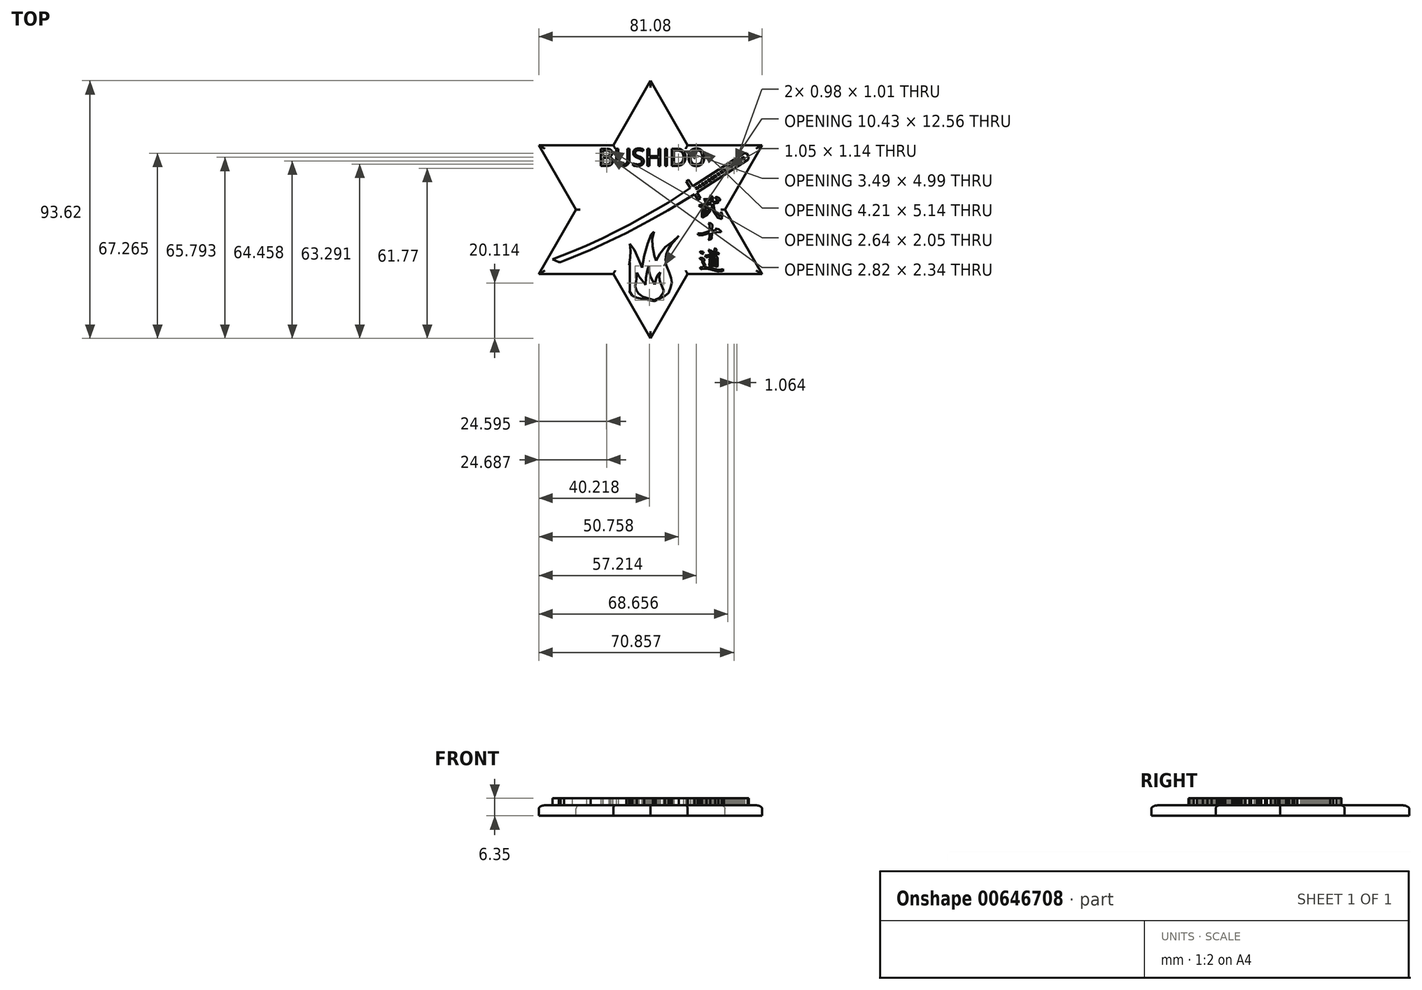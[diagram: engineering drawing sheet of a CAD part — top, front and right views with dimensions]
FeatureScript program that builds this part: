
annotation { "Feature Type Name" : "Feature", "Feature Type Description" : "" }
export const myFeature = defineFeature(function(context is Context, id is Id, definition is map)
    precondition{}
    {
        {
            var Q0;
            Q0=qCreatedBy(makeId("Top.planeOp"),FACE);
            var sketch = newSketch(context, id + "F0", { "sketchPlane" : qUnion([Q0])});
            skLineSegment(sketch, "E0.0", {"start": v(40.54, -23.4) * mm, "end": v(13.51, -23.4) * mm});
            skLineSegment(sketch, "E0.1", {"start": v(-40.54, -23.4) * mm, "end": v(-27.02, 0) * mm});
            skLineSegment(sketch, "E0.2", {"start": v(0, 46.8) * mm, "end": v(13.51, 23.4) * mm});
            skPoint(sketch, "E0.0.midPoint", {"position": v(0, -23.4) * mm});
            skLineSegment(sketch, "E1.0", {"start": v(-40.54, 23.4) * mm, "end": v(-13.51, 23.4) * mm});
            skLineSegment(sketch, "E1.1", {"start": v(40.54, 23.4) * mm, "end": v(27.02, 0) * mm});
            skLineSegment(sketch, "E1.2", {"start": v(0, -46.8) * mm, "end": v(-13.51, -23.4) * mm});
            skPoint(sketch, "E1.0.midPoint", {"position": v(0, 23.4) * mm});
            skPoint(sketch, "E0.cCircle.center.orphan", {"position": v(0, 0) * mm});
            skLineSegment(sketch, "E2.trimOffspring", {"start": v(13.51, -23.4) * mm, "end": v(0, -46.8) * mm});
            skLineSegment(sketch, "E3.trimOffspring", {"start": v(27.02, 0) * mm, "end": v(40.54, -23.4) * mm});
            skLineSegment(sketch, "E4.trimOffspring", {"start": v(13.51, 23.4) * mm, "end": v(40.54, 23.4) * mm});
            skLineSegment(sketch, "E5.trimOffspring", {"start": v(-13.51, 23.4) * mm, "end": v(0, 46.8) * mm});
            skLineSegment(sketch, "E6.trimOffspring", {"start": v(-27.02, 0) * mm, "end": v(-40.54, 23.4) * mm});
            skLineSegment(sketch, "E7.trimOffspring", {"start": v(-13.51, -23.4) * mm, "end": v(-40.54, -23.4) * mm});
            skSolve(sketch);
        }
        {
            var Q0;
            Q0=qCreatedBy(makeId("Top.planeOp"),FACE);
            var sketch = newSketch(context, id + "F1", { "sketchPlane" : qUnion([Q0])});
            skText(sketch, "E8", { "text": "BUSHIDO", "fontName": "OpenSans-Regular.ttf"});
            const initialGuessF1  = {"E8": [-0.01885, 0.01586, 1, 0, 0.0063]};
            skSetInitialGuess(sketch, initialGuessF1);
            skSolve(sketch);
        }
        {
            var Q0;
            Q0=qCreatedBy(makeId("Top.planeOp"),FACE);
            var sketch = newSketch(context, id + "F2", { "sketchPlane" : qUnion([Q0])});
            skLineSegment(sketch, "E9", {"start": v(15.34, 8.47) * mm, "end": v(33.88, 20.46) * mm});
            skLineSegment(sketch, "E10", {"start": v(33.88, 20.46) * mm, "end": v(34.92, 20.37) * mm});
            skLineSegment(sketch, "E11", {"start": v(34.92, 20.37) * mm, "end": v(35.66, 19.22) * mm});
            skLineSegment(sketch, "E12", {"start": v(35.66, 19.22) * mm, "end": v(35.4, 18.12) * mm});
            skLineSegment(sketch, "E13", {"start": v(35.4, 18.12) * mm, "end": v(16.85, 6.14) * mm});
            skLineSegment(sketch, "E14", {"start": v(12.95, 10.24) * mm, "end": v(13.83, 10.8) * mm});
            skLineSegment(sketch, "E15", {"start": v(13.83, 10.8) * mm, "end": v(18.2, 4.04) * mm});
            skLineSegment(sketch, "E16", {"start": v(18.2, 4.04) * mm, "end": v(17.3, 3.5) * mm});
            skLineSegment(sketch, "E17", {"start": v(17.3, 3.5) * mm, "end": v(12.95, 10.24) * mm});
            skLineSegment(sketch, "E18", {"start": v(16.55, 8.25) * mm, "end": v(16.34, 7.6) * mm});
            skLineSegment(sketch, "E19", {"start": v(16.34, 7.6) * mm, "end": v(17.21, 7.33) * mm});
            skLineSegment(sketch, "E20", {"start": v(17.21, 7.33) * mm, "end": v(17.4, 7.9) * mm});
            skLineSegment(sketch, "E21", {"start": v(17.4, 7.9) * mm, "end": v(16.55, 8.25) * mm});
            skLineSegment(sketch, "E22", {"start": v(17.65, 8.97) * mm, "end": v(17.54, 8.22) * mm});
            skLineSegment(sketch, "E23", {"start": v(17.54, 8.22) * mm, "end": v(18.43, 8.09) * mm});
            skLineSegment(sketch, "E24", {"start": v(18.43, 8.09) * mm, "end": v(18.51, 8.64) * mm});
            skLineSegment(sketch, "E25", {"start": v(18.51, 8.64) * mm, "end": v(17.65, 8.97) * mm});
            skLineSegment(sketch, "E26", {"start": v(18.82, 9.72) * mm, "end": v(18.74, 8.83) * mm});
            skLineSegment(sketch, "E27", {"start": v(18.74, 8.83) * mm, "end": v(19.57, 8.76) * mm});
            skLineSegment(sketch, "E28", {"start": v(19.57, 8.76) * mm, "end": v(19.62, 9.43) * mm});
            skLineSegment(sketch, "E29", {"start": v(19.62, 9.43) * mm, "end": v(18.82, 9.72) * mm});
            skLineSegment(sketch, "E30", {"start": v(19.9, 10.43) * mm, "end": v(19.88, 9.68) * mm});
            skLineSegment(sketch, "E31", {"start": v(19.88, 9.68) * mm, "end": v(20.51, 9.4) * mm});
            skLineSegment(sketch, "E32", {"start": v(20.51, 9.4) * mm, "end": v(20.58, 10.1) * mm});
            skLineSegment(sketch, "E33", {"start": v(20.58, 10.1) * mm, "end": v(19.9, 10.43) * mm});
            skLineSegment(sketch, "E34", {"start": v(21.02, 11.14) * mm, "end": v(20.9, 10.44) * mm});
            skLineSegment(sketch, "E35", {"start": v(20.9, 10.44) * mm, "end": v(21.67, 10.1) * mm});
            skLineSegment(sketch, "E36", {"start": v(21.67, 10.1) * mm, "end": v(21.93, 10.69) * mm});
            skLineSegment(sketch, "E37", {"start": v(21.93, 10.69) * mm, "end": v(21.02, 11.14) * mm});
            skLineSegment(sketch, "E38", {"start": v(22.13, 11.86) * mm, "end": v(21.96, 11.15) * mm});
            skLineSegment(sketch, "E39", {"start": v(21.96, 11.15) * mm, "end": v(22.82, 10.95) * mm});
            skLineSegment(sketch, "E40", {"start": v(22.82, 10.95) * mm, "end": v(22.97, 11.51) * mm});
            skLineSegment(sketch, "E41", {"start": v(22.97, 11.51) * mm, "end": v(22.13, 11.86) * mm});
            skLineSegment(sketch, "E42", {"start": v(23.24, 12.58) * mm, "end": v(23.05, 11.94) * mm});
            skLineSegment(sketch, "E43", {"start": v(23.05, 11.94) * mm, "end": v(23.85, 11.7) * mm});
            skLineSegment(sketch, "E44", {"start": v(23.85, 11.7) * mm, "end": v(24, 12.2) * mm});
            skLineSegment(sketch, "E45", {"start": v(24, 12.2) * mm, "end": v(23.24, 12.58) * mm});
            skLineSegment(sketch, "E46", {"start": v(24.42, 13.34) * mm, "end": v(24.27, 12.62) * mm});
            skLineSegment(sketch, "E47", {"start": v(24.27, 12.62) * mm, "end": v(25, 12.46) * mm});
            skLineSegment(sketch, "E48", {"start": v(25, 12.46) * mm, "end": v(25.16, 12.95) * mm});
            skLineSegment(sketch, "E49", {"start": v(25.16, 12.95) * mm, "end": v(24.42, 13.34) * mm});
            skLineSegment(sketch, "E50", {"start": v(25.56, 14.13) * mm, "end": v(25.36, 13.44) * mm});
            skLineSegment(sketch, "E51", {"start": v(25.36, 13.44) * mm, "end": v(26.18, 13.2) * mm});
            skLineSegment(sketch, "E52", {"start": v(26.18, 13.2) * mm, "end": v(26.34, 13.78) * mm});
            skLineSegment(sketch, "E53", {"start": v(26.34, 13.78) * mm, "end": v(25.56, 14.13) * mm});
            skLineSegment(sketch, "E54", {"start": v(26.77, 14.86) * mm, "end": v(26.5, 14.15) * mm});
            skLineSegment(sketch, "E55", {"start": v(26.5, 14.15) * mm, "end": v(27.17, 13.9) * mm});
            skLineSegment(sketch, "E56", {"start": v(27.17, 13.9) * mm, "end": v(27.39, 14.47) * mm});
            skLineSegment(sketch, "E57", {"start": v(27.39, 14.47) * mm, "end": v(26.77, 14.86) * mm});
            skLineSegment(sketch, "E58", {"start": v(27.8, 15.53) * mm, "end": v(27.6, 14.77) * mm});
            skLineSegment(sketch, "E59", {"start": v(27.6, 14.77) * mm, "end": v(28.27, 14.4) * mm});
            skLineSegment(sketch, "E60", {"start": v(28.27, 14.4) * mm, "end": v(28.64, 15.06) * mm});
            skLineSegment(sketch, "E61", {"start": v(28.64, 15.06) * mm, "end": v(27.8, 15.53) * mm});
            skLineSegment(sketch, "E62", {"start": v(28.9, 16.23) * mm, "end": v(28.62, 15.49) * mm});
            skLineSegment(sketch, "E63", {"start": v(28.62, 15.49) * mm, "end": v(29.33, 15.22) * mm});
            skLineSegment(sketch, "E64", {"start": v(29.33, 15.22) * mm, "end": v(29.57, 15.87) * mm});
            skLineSegment(sketch, "E65", {"start": v(29.57, 15.87) * mm, "end": v(28.9, 16.23) * mm});
            skLineSegment(sketch, "E66", {"start": v(30.06, 16.99) * mm, "end": v(29.83, 16.21) * mm});
            skLineSegment(sketch, "E67", {"start": v(29.83, 16.21) * mm, "end": v(30.61, 15.98) * mm});
            skLineSegment(sketch, "E68", {"start": v(30.61, 15.98) * mm, "end": v(30.8, 16.62) * mm});
            skLineSegment(sketch, "E69", {"start": v(30.8, 16.62) * mm, "end": v(30.06, 16.99) * mm});
            skLineSegment(sketch, "E70", {"start": v(31.23, 17.74) * mm, "end": v(30.89, 17.09) * mm});
            skLineSegment(sketch, "E71", {"start": v(30.89, 17.09) * mm, "end": v(31.59, 16.73) * mm});
            skLineSegment(sketch, "E72", {"start": v(31.59, 16.73) * mm, "end": v(31.87, 17.27) * mm});
            skLineSegment(sketch, "E73", {"start": v(31.87, 17.27) * mm, "end": v(31.23, 17.74) * mm});
            skLineSegment(sketch, "E74", {"start": v(32.3, 18.43) * mm, "end": v(31.96, 17.78) * mm});
            skLineSegment(sketch, "E75", {"start": v(31.96, 17.78) * mm, "end": v(32.67, 17.4) * mm});
            skLineSegment(sketch, "E76", {"start": v(32.67, 17.4) * mm, "end": v(32.98, 17.98) * mm});
            skLineSegment(sketch, "E77", {"start": v(32.98, 17.98) * mm, "end": v(32.3, 18.43) * mm});
            skPoint(sketch, "E78.orphan", {"position": v(32.32, 18.44) * mm});
            skLineSegment(sketch, "E79", {"start": v(33.35, 19.2) * mm, "end": v(33.15, 18.54) * mm});
            skPoint(sketch, "E79.endSnap0", {"position": v(31.55, 17.5) * mm});
            skLineSegment(sketch, "E80", {"start": v(33.15, 18.54) * mm, "end": v(33.88, 18.06) * mm});
            skLineSegment(sketch, "E81", {"start": v(33.88, 18.06) * mm, "end": v(34.12, 18.82) * mm});
            skLineSegment(sketch, "E82", {"start": v(34.12, 18.82) * mm, "end": v(33.35, 19.2) * mm});
            skLineSegment(sketch, "E83", {"start": v(14.46, 7.9) * mm, "end": v(13.44, 5.95) * mm});
            skLineSegment(sketch, "E84", {"start": v(13.44, 5.95) * mm, "end": v(15.97, 5.57) * mm});
            skLineSegment(sketch, "E85", {"start": v(15.97, 5.57) * mm, "end": v(13.5, 3.98) * mm});
            skLineSegment(sketch, "E86", {"start": v(13.5, 3.98) * mm, "end": v(6.4, -0.24) * mm});
            skLineSegment(sketch, "E87", {"start": v(6.4, -0.24) * mm, "end": v(0.58, -3.5) * mm});
            skLineSegment(sketch, "E88", {"start": v(0.58, -3.5) * mm, "end": v(-8.8, -8.5) * mm});
            skLineSegment(sketch, "E89", {"start": v(-8.8, -8.5) * mm, "end": v(-21.7, -14.6) * mm});
            skLineSegment(sketch, "E90", {"start": v(-21.7, -14.6) * mm, "end": v(-31.4, -18.56) * mm});
            skLineSegment(sketch, "E91", {"start": v(-31.4, -18.56) * mm, "end": v(-32.66, -19.03) * mm});
            skLineSegment(sketch, "E92", {"start": v(-32.66, -19.03) * mm, "end": v(-33.3, -19.1) * mm});
            skLineSegment(sketch, "E93", {"start": v(-33.3, -19.1) * mm, "end": v(-35.54, -18.07) * mm});
            skLineSegment(sketch, "E94", {"start": v(-35.54, -18.07) * mm, "end": v(-28.42, -15.3) * mm});
            skLineSegment(sketch, "E95", {"start": v(-28.42, -15.3) * mm, "end": v(-23.22, -13.07) * mm});
            skLineSegment(sketch, "E96", {"start": v(-23.22, -13.07) * mm, "end": v(-17.44, -10.38) * mm});
            skLineSegment(sketch, "E97", {"start": v(-17.44, -10.38) * mm, "end": v(-12.94, -8.11) * mm});
            skLineSegment(sketch, "E98", {"start": v(-12.94, -8.11) * mm, "end": v(-7.67, -5.44) * mm});
            skLineSegment(sketch, "E99", {"start": v(-7.67, -5.44) * mm, "end": v(-3.24, -2.96) * mm});
            skLineSegment(sketch, "E100", {"start": v(-3.24, -2.96) * mm, "end": v(2.18, 0.08) * mm});
            skLineSegment(sketch, "E101", {"start": v(2.18, 0.08) * mm, "end": v(6.48, 2.49) * mm});
            skLineSegment(sketch, "E102", {"start": v(6.48, 2.49) * mm, "end": v(14.46, 7.9) * mm});
            skLineSegment(sketch, "E103", {"start": v(13.44, 5.95) * mm, "end": v(7.48, 2.47) * mm});
            skLineSegment(sketch, "E104", {"start": v(7.48, 2.47) * mm, "end": v(0.03, -1.9) * mm});
            skLineSegment(sketch, "E105", {"start": v(0.03, -1.9) * mm, "end": v(-3.12, -3.67) * mm});
            skLineSegment(sketch, "E106", {"start": v(-3.12, -3.67) * mm, "end": v(-6.95, -5.81) * mm});
            skLineSegment(sketch, "E107", {"start": v(-6.95, -5.81) * mm, "end": v(-10.18, -7.44) * mm});
            skLineSegment(sketch, "E108", {"start": v(-10.18, -7.44) * mm, "end": v(-13.58, -9.15) * mm});
            skLineSegment(sketch, "E109", {"start": v(-13.58, -9.15) * mm, "end": v(-19.43, -12.06) * mm});
            skLineSegment(sketch, "E110", {"start": v(-19.43, -12.06) * mm, "end": v(-23.74, -14.07) * mm});
            skLineSegment(sketch, "E111", {"start": v(-23.74, -14.07) * mm, "end": v(-29.14, -16.33) * mm});
            skLineSegment(sketch, "E112", {"start": v(-29.14, -16.33) * mm, "end": v(-32.88, -17.72) * mm});
            skLineSegment(sketch, "E113", {"start": v(-32.88, -17.72) * mm, "end": v(-35.54, -18.07) * mm});
            skLineSegment(sketch, "E114.0", {"start": v(14.46, 7.9) * mm, "end": v(15.34, 8.47) * mm, "construction": true});
            skLineSegment(sketch, "E115.0", {"start": v(16.55, 8.25) * mm, "end": v(32.32, 18.44) * mm, "construction": true});
            skLineSegment(sketch, "E116.0", {"start": v(31.55, 17.5) * mm, "end": v(33.15, 18.54) * mm, "construction": true});
            skLineSegment(sketch, "E117.0", {"start": v(15.97, 5.57) * mm, "end": v(16.85, 6.14) * mm, "construction": true});
            skLineSegment(sketch, "E118.0", {"start": v(7.48, 2.47) * mm, "end": v(33.35, 19.2) * mm, "construction": true});
            skLineSegment(sketch, "E119.0", {"start": v(-10.18, -7.44) * mm, "end": v(-3.24, -2.96) * mm, "construction": true});
            skLineSegment(sketch, "E120.0", {"start": v(15.34, 8.47) * mm, "end": v(13.83, 10.8) * mm, "construction": true});
            skLineSegment(sketch, "E121.0", {"start": v(17.3, 3.5) * mm, "end": v(12.95, 10.24) * mm, "construction": true});
            skSolve(sketch);
        }
        {
            var Q0;
            Q0=qCreatedBy(makeId("Top.planeOp"),FACE);
            var sketch = newSketch(context, id + "F3", { "sketchPlane" : qUnion([Q0])});
            skFitSpline(sketch, "E122", {"points": [v(19.27, 3.7) * mm, v(21.47, 3.65) * mm, v(19.77, 2.87) * mm, v(20.16, 3.2) * mm, v(19.27, 3.7) * mm]});
            skFitSpline(sketch, "E123", {"points": [v(23.53, 4.38) * mm, v(25, 3.2) * mm, v(25.02, 4.08) * mm, v(23.53, 4.38) * mm]});
            skLineSegment(sketch, "E124", {"start": v(21.52, 5.11) * mm, "end": v(22.2, 4.96) * mm});
            skLineSegment(sketch, "E125", {"start": v(22.2, 4.96) * mm, "end": v(22.65, 4.52) * mm});
            skLineSegment(sketch, "E126", {"start": v(22.65, 4.52) * mm, "end": v(22.65, 2.8) * mm});
            skLineSegment(sketch, "E127", {"start": v(22.65, 2.8) * mm, "end": v(24.31, 3.08) * mm});
            skLineSegment(sketch, "E128", {"start": v(24.31, 3.08) * mm, "end": v(24.79, 2.72) * mm});
            skLineSegment(sketch, "E129", {"start": v(24.79, 2.72) * mm, "end": v(24.2, 2.4) * mm});
            skLineSegment(sketch, "E130", {"start": v(24.2, 2.4) * mm, "end": v(22.86, 2.14) * mm});
            skLineSegment(sketch, "E131", {"start": v(22.86, 2.14) * mm, "end": v(23.31, -0.3) * mm});
            skLineSegment(sketch, "E132", {"start": v(23.31, -0.3) * mm, "end": v(25.29, -2.58) * mm});
            skLineSegment(sketch, "E133", {"start": v(25.29, -2.58) * mm, "end": v(25.61, -1.7) * mm});
            skLineSegment(sketch, "E134", {"start": v(25.61, -1.7) * mm, "end": v(25.61, -0.75) * mm});
            skLineSegment(sketch, "E135", {"start": v(25.61, -0.75) * mm, "end": v(26.1, -1.82) * mm});
            skLineSegment(sketch, "E136", {"start": v(26.1, -1.82) * mm, "end": v(25.88, -3.5) * mm});
            skLineSegment(sketch, "E137", {"start": v(25.88, -3.5) * mm, "end": v(24.4, -2.9) * mm});
            skLineSegment(sketch, "E138", {"start": v(24.4, -2.9) * mm, "end": v(22.74, -0.5) * mm});
            skLineSegment(sketch, "E139", {"start": v(22.74, -0.5) * mm, "end": v(22.1, 2.05) * mm});
            skLineSegment(sketch, "E140", {"start": v(22.1, 2.05) * mm, "end": v(20.23, 1.58) * mm});
            skLineSegment(sketch, "E141", {"start": v(20.23, 1.58) * mm, "end": v(20.37, 1.01) * mm});
            skLineSegment(sketch, "E142", {"start": v(20.37, 1.01) * mm, "end": v(20.75, 0.63) * mm});
            skLineSegment(sketch, "E143", {"start": v(20.75, 0.63) * mm, "end": v(20.75, 0.29) * mm});
            skLineSegment(sketch, "E144", {"start": v(20.75, 0.29) * mm, "end": v(21.44, 0.5) * mm});
            skLineSegment(sketch, "E145", {"start": v(21.44, 0.5) * mm, "end": v(21.98, 0.5) * mm});
            skLineSegment(sketch, "E146", {"start": v(21.98, 0.5) * mm, "end": v(21.61, -0.11) * mm});
            skLineSegment(sketch, "E147", {"start": v(21.61, -0.11) * mm, "end": v(20.71, -0.11) * mm});
            skLineSegment(sketch, "E148", {"start": v(20.71, -0.11) * mm, "end": v(20.5, -1.26) * mm});
            skLineSegment(sketch, "E149", {"start": v(20.5, -1.26) * mm, "end": v(21.29, -0.9) * mm});
            skLineSegment(sketch, "E150", {"start": v(21.29, -0.9) * mm, "end": v(21.88, -0.4) * mm});
            skLineSegment(sketch, "E151", {"start": v(21.88, -0.4) * mm, "end": v(20.5, -2.1) * mm});
            skLineSegment(sketch, "E152", {"start": v(20.5, -2.1) * mm, "end": v(18.86, -2.9) * mm});
            skLineSegment(sketch, "E153", {"start": v(18.86, -2.9) * mm, "end": v(18.65, -2.49) * mm});
            skLineSegment(sketch, "E154", {"start": v(18.65, -2.49) * mm, "end": v(18.65, -1.78) * mm});
            skLineSegment(sketch, "E155", {"start": v(18.65, -1.78) * mm, "end": v(18.82, 0.13) * mm});
            skLineSegment(sketch, "E156", {"start": v(18.82, 0.13) * mm, "end": v(18.82, 0.69) * mm});
            skLineSegment(sketch, "E157", {"start": v(18.82, 0.69) * mm, "end": v(19.22, 0.23) * mm});
            skLineSegment(sketch, "E158", {"start": v(19.22, 0.23) * mm, "end": v(19.35, -0.32) * mm});
            skLineSegment(sketch, "E159", {"start": v(19.35, -0.32) * mm, "end": v(19.05, -2.05) * mm});
            skLineSegment(sketch, "E160", {"start": v(19.05, -2.05) * mm, "end": v(20.04, -1.66) * mm});
            skLineSegment(sketch, "E161", {"start": v(20.04, -1.66) * mm, "end": v(20.04, 0.25) * mm});
            skLineSegment(sketch, "E162", {"start": v(20.04, 0.25) * mm, "end": v(19.87, 1.44) * mm});
            skLineSegment(sketch, "E163", {"start": v(19.87, 1.44) * mm, "end": v(18.82, 1.02) * mm});
            skLineSegment(sketch, "E164", {"start": v(18.82, 1.02) * mm, "end": v(18.05, 1.02) * mm});
            skLineSegment(sketch, "E165", {"start": v(18.05, 1.02) * mm, "end": v(17.57, 1.55) * mm});
            skLineSegment(sketch, "E166", {"start": v(17.57, 1.55) * mm, "end": v(18.34, 1.72) * mm});
            skLineSegment(sketch, "E167", {"start": v(18.34, 1.72) * mm, "end": v(22.09, 2.7) * mm});
            skLineSegment(sketch, "E168", {"start": v(22.09, 2.7) * mm, "end": v(21.88, 4.58) * mm});
            skLineSegment(sketch, "E169", {"start": v(21.88, 4.58) * mm, "end": v(21.52, 5.11) * mm});
            skLineSegment(sketch, "E170", {"start": v(21.06, -5) * mm, "end": v(21.52, -4.85) * mm});
            skLineSegment(sketch, "E171", {"start": v(21.52, -4.85) * mm, "end": v(21.88, -5) * mm});
            skLineSegment(sketch, "E172", {"start": v(21.88, -5) * mm, "end": v(22.5, -5.54) * mm});
            skLineSegment(sketch, "E173", {"start": v(22.5, -5.54) * mm, "end": v(22.35, -7.68) * mm});
            skLineSegment(sketch, "E174", {"start": v(22.35, -7.68) * mm, "end": v(24.07, -7.44) * mm});
            skLineSegment(sketch, "E175", {"start": v(24.07, -7.44) * mm, "end": v(23.88, -7.36) * mm});
            skLineSegment(sketch, "E176", {"start": v(23.88, -7.36) * mm, "end": v(23.53, -6.94) * mm});
            skLineSegment(sketch, "E177", {"start": v(23.53, -6.94) * mm, "end": v(24.75, -7.1) * mm});
            skLineSegment(sketch, "E178", {"start": v(24.75, -7.1) * mm, "end": v(25.67, -7.92) * mm});
            skLineSegment(sketch, "E179", {"start": v(25.67, -7.92) * mm, "end": v(25.67, -8.16) * mm});
            skLineSegment(sketch, "E180", {"start": v(25.67, -8.16) * mm, "end": v(22.37, -8.37) * mm});
            skLineSegment(sketch, "E181", {"start": v(22.37, -8.37) * mm, "end": v(22.2, -10.58) * mm});
            skLineSegment(sketch, "E182", {"start": v(22.2, -10.58) * mm, "end": v(21.8, -10.82) * mm});
            skLineSegment(sketch, "E183", {"start": v(21.8, -10.82) * mm, "end": v(20.92, -11.08) * mm});
            skLineSegment(sketch, "E184", {"start": v(20.92, -11.08) * mm, "end": v(21.37, -10.6) * mm});
            skLineSegment(sketch, "E185", {"start": v(21.37, -10.6) * mm, "end": v(21.5, -9.58) * mm});
            skLineSegment(sketch, "E186", {"start": v(21.5, -9.58) * mm, "end": v(21.5, -8.53) * mm});
            skLineSegment(sketch, "E187", {"start": v(21.5, -8.53) * mm, "end": v(18.97, -9.32) * mm});
            skLineSegment(sketch, "E188", {"start": v(18.97, -9.32) * mm, "end": v(18.07, -9.32) * mm});
            skLineSegment(sketch, "E189", {"start": v(18.07, -9.32) * mm, "end": v(17.45, -9.24) * mm});
            skLineSegment(sketch, "E190", {"start": v(17.45, -9.24) * mm, "end": v(17.18, -8.71) * mm});
            skLineSegment(sketch, "E191", {"start": v(17.18, -8.71) * mm, "end": v(19.16, -8.5) * mm});
            skLineSegment(sketch, "E192", {"start": v(19.16, -8.5) * mm, "end": v(21.52, -7.8) * mm});
            skLineSegment(sketch, "E193", {"start": v(21.52, -7.8) * mm, "end": v(21.52, -5.76) * mm});
            skLineSegment(sketch, "E194", {"start": v(21.52, -5.76) * mm, "end": v(21.06, -5) * mm});
            skLineSegment(sketch, "E195", {"start": v(19.08, -11.44) * mm, "end": v(21.42, -11.17) * mm});
            skLineSegment(sketch, "E196", {"start": v(21.42, -11.17) * mm, "end": v(22.78, -10.96) * mm});
            skLineSegment(sketch, "E197", {"start": v(22.78, -10.96) * mm, "end": v(23.37, -10.8) * mm});
            skLineSegment(sketch, "E198", {"start": v(23.37, -10.8) * mm, "end": v(23.77, -10.83) * mm});
            skLineSegment(sketch, "E199", {"start": v(23.77, -10.83) * mm, "end": v(24.27, -11.03) * mm});
            skLineSegment(sketch, "E200", {"start": v(24.27, -11.03) * mm, "end": v(24.49, -11.57) * mm});
            skLineSegment(sketch, "E201", {"start": v(24.49, -11.57) * mm, "end": v(23.88, -11.57) * mm});
            skLineSegment(sketch, "E202", {"start": v(23.88, -11.57) * mm, "end": v(22.97, -11.57) * mm});
            skLineSegment(sketch, "E203", {"start": v(22.97, -11.57) * mm, "end": v(22.03, -11.57) * mm});
            skLineSegment(sketch, "E204", {"start": v(22.03, -11.57) * mm, "end": v(20.65, -11.88) * mm});
            skLineSegment(sketch, "E205", {"start": v(20.65, -11.88) * mm, "end": v(19.79, -12.03) * mm});
            skLineSegment(sketch, "E206", {"start": v(19.79, -12.03) * mm, "end": v(19.46, -11.88) * mm});
            skLineSegment(sketch, "E207", {"start": v(19.46, -11.88) * mm, "end": v(19.07, -11.47) * mm});
            skLineSegment(sketch, "E208", {"start": v(17.98, -15.17) * mm, "end": v(18.86, -15.28) * mm});
            skLineSegment(sketch, "E209", {"start": v(18.86, -15.28) * mm, "end": v(19.2, -15.45) * mm});
            skLineSegment(sketch, "E210", {"start": v(19.2, -15.45) * mm, "end": v(19.31, -15.9) * mm});
            skLineSegment(sketch, "E211", {"start": v(19.31, -15.9) * mm, "end": v(18.54, -16.21) * mm});
            skLineSegment(sketch, "E212", {"start": v(18.54, -16.21) * mm, "end": v(18.51, -16) * mm});
            skLineSegment(sketch, "E213", {"start": v(18.51, -16) * mm, "end": v(18.7, -15.96) * mm});
            skLineSegment(sketch, "E214", {"start": v(18.7, -15.96) * mm, "end": v(18.08, -15.61) * mm});
            skLineSegment(sketch, "E215", {"start": v(18.08, -15.61) * mm, "end": v(17.98, -15.17) * mm});
            skLineSegment(sketch, "E216", {"start": v(21.52, -14.47) * mm, "end": v(21.58, -14.74) * mm});
            skLineSegment(sketch, "E217", {"start": v(21.58, -14.74) * mm, "end": v(21.88, -15.11) * mm});
            skLineSegment(sketch, "E218", {"start": v(21.88, -15.11) * mm, "end": v(22.42, -14.77) * mm});
            skLineSegment(sketch, "E219", {"start": v(22.42, -14.77) * mm, "end": v(21.98, -15.86) * mm});
            skLineSegment(sketch, "E220", {"start": v(21.98, -15.86) * mm, "end": v(21.43, -15.49) * mm});
            skLineSegment(sketch, "E221", {"start": v(21.43, -15.49) * mm, "end": v(21.2, -15.04) * mm});
            skLineSegment(sketch, "E222", {"start": v(21.2, -15.04) * mm, "end": v(21.2, -14.66) * mm});
            skLineSegment(sketch, "E223", {"start": v(21.2, -14.66) * mm, "end": v(21.52, -14.47) * mm});
            skLineSegment(sketch, "E224", {"start": v(23.3, -14.14) * mm, "end": v(23.76, -14.2) * mm});
            skLineSegment(sketch, "E225", {"start": v(23.76, -14.2) * mm, "end": v(24.04, -14.62) * mm});
            skLineSegment(sketch, "E226", {"start": v(24.04, -14.62) * mm, "end": v(24.1, -14.88) * mm});
            skLineSegment(sketch, "E227", {"start": v(24.1, -14.88) * mm, "end": v(23.06, -15.69) * mm});
            skLineSegment(sketch, "E228", {"start": v(23.06, -15.69) * mm, "end": v(22.18, -16.07) * mm});
            skLineSegment(sketch, "E229", {"start": v(22.18, -16.07) * mm, "end": v(22.56, -16.12) * mm});
            skLineSegment(sketch, "E230", {"start": v(22.56, -16.12) * mm, "end": v(23.62, -15.75) * mm});
            skLineSegment(sketch, "E231", {"start": v(23.62, -15.75) * mm, "end": v(24.41, -15.66) * mm});
            skLineSegment(sketch, "E232", {"start": v(24.41, -15.66) * mm, "end": v(24.71, -15.78) * mm});
            skLineSegment(sketch, "E233", {"start": v(24.71, -15.78) * mm, "end": v(25.06, -16.12) * mm});
            skLineSegment(sketch, "E234", {"start": v(25.06, -16.12) * mm, "end": v(22.56, -16.47) * mm});
            skLineSegment(sketch, "E235", {"start": v(22.56, -16.47) * mm, "end": v(22.5, -17.15) * mm});
            skLineSegment(sketch, "E236", {"start": v(22.5, -17.15) * mm, "end": v(22.4, -17.3) * mm});
            skLineSegment(sketch, "E237", {"start": v(22.4, -17.3) * mm, "end": v(23.1, -17.09) * mm});
            skLineSegment(sketch, "E238", {"start": v(23.1, -17.09) * mm, "end": v(23.92, -16.97) * mm});
            skLineSegment(sketch, "E239", {"start": v(23.92, -16.97) * mm, "end": v(24.36, -17.46) * mm});
            skLineSegment(sketch, "E240", {"start": v(24.36, -17.46) * mm, "end": v(24.45, -19.91) * mm});
            skLineSegment(sketch, "E241", {"start": v(24.45, -19.91) * mm, "end": v(24.4, -20.27) * mm});
            skLineSegment(sketch, "E242", {"start": v(24.4, -20.27) * mm, "end": v(24.12, -20.97) * mm});
            skLineSegment(sketch, "E243", {"start": v(24.12, -20.97) * mm, "end": v(23.76, -20.55) * mm});
            skLineSegment(sketch, "E244", {"start": v(23.76, -20.55) * mm, "end": v(23.76, -18.48) * mm});
            skLineSegment(sketch, "E245", {"start": v(23.76, -18.48) * mm, "end": v(23.76, -17.97) * mm});
            skLineSegment(sketch, "E246", {"start": v(23.76, -17.97) * mm, "end": v(23.6, -17.5) * mm});
            skLineSegment(sketch, "E247", {"start": v(23.6, -17.5) * mm, "end": v(23.12, -17.61) * mm});
            skLineSegment(sketch, "E248", {"start": v(23.12, -17.61) * mm, "end": v(22.47, -17.53) * mm});
            skLineSegment(sketch, "E249", {"start": v(22.47, -17.53) * mm, "end": v(22.05, -17.53) * mm});
            skLineSegment(sketch, "E250", {"start": v(22.05, -17.53) * mm, "end": v(21.78, -17.7) * mm});
            skLineSegment(sketch, "E251", {"start": v(21.78, -17.7) * mm, "end": v(21.88, -18.1) * mm});
            skLineSegment(sketch, "E252", {"start": v(21.88, -18.1) * mm, "end": v(21.91, -18.18) * mm});
            skLineSegment(sketch, "E253", {"start": v(21.91, -18.18) * mm, "end": v(22.47, -18.1) * mm});
            skLineSegment(sketch, "E254", {"start": v(22.47, -18.1) * mm, "end": v(22.94, -18) * mm});
            skLineSegment(sketch, "E255", {"start": v(22.94, -18) * mm, "end": v(23.21, -18.02) * mm});
            skLineSegment(sketch, "E256", {"start": v(23.21, -18.02) * mm, "end": v(23.4, -18.2) * mm});
            skLineSegment(sketch, "E257", {"start": v(23.4, -18.2) * mm, "end": v(23.17, -18.41) * mm});
            skLineSegment(sketch, "E258", {"start": v(23.17, -18.41) * mm, "end": v(22.62, -18.6) * mm});
            skLineSegment(sketch, "E259", {"start": v(22.62, -18.6) * mm, "end": v(22.35, -18.8) * mm});
            skLineSegment(sketch, "E260", {"start": v(22.35, -18.8) * mm, "end": v(22.28, -18.74) * mm});
            skLineSegment(sketch, "E261", {"start": v(22.28, -18.74) * mm, "end": v(22.47, -18.58) * mm});
            skLineSegment(sketch, "E262", {"start": v(22.47, -18.58) * mm, "end": v(22.36, -18.54) * mm});
            skLineSegment(sketch, "E263", {"start": v(22.36, -18.54) * mm, "end": v(21.85, -18.53) * mm});
            skLineSegment(sketch, "E264", {"start": v(21.85, -18.53) * mm, "end": v(21.85, -19.04) * mm});
            skLineSegment(sketch, "E265", {"start": v(21.85, -19.04) * mm, "end": v(22.27, -19.04) * mm});
            skLineSegment(sketch, "E266", {"start": v(22.27, -19.04) * mm, "end": v(22.96, -18.88) * mm});
            skLineSegment(sketch, "E267", {"start": v(22.96, -18.88) * mm, "end": v(23.31, -18.88) * mm});
            skLineSegment(sketch, "E268", {"start": v(23.31, -18.88) * mm, "end": v(23.5, -19.03) * mm});
            skLineSegment(sketch, "E269", {"start": v(23.5, -19.03) * mm, "end": v(23.41, -19.26) * mm});
            skLineSegment(sketch, "E270", {"start": v(23.41, -19.26) * mm, "end": v(22.9, -19.5) * mm});
            skLineSegment(sketch, "E271", {"start": v(22.9, -19.5) * mm, "end": v(22.54, -19.75) * mm});
            skLineSegment(sketch, "E272", {"start": v(22.54, -19.75) * mm, "end": v(22.5, -19.7) * mm});
            skLineSegment(sketch, "E273", {"start": v(22.5, -19.7) * mm, "end": v(22.8, -19.38) * mm});
            skLineSegment(sketch, "E274", {"start": v(22.8, -19.38) * mm, "end": v(21.9, -19.3) * mm});
            skLineSegment(sketch, "E275", {"start": v(21.9, -19.3) * mm, "end": v(21.83, -19.49) * mm});
            skLineSegment(sketch, "E276", {"start": v(21.83, -19.49) * mm, "end": v(21.79, -20.08) * mm});
            skLineSegment(sketch, "E277", {"start": v(21.79, -20.08) * mm, "end": v(22.08, -19.96) * mm});
            skLineSegment(sketch, "E278", {"start": v(22.08, -19.96) * mm, "end": v(22.06, -20.03) * mm});
            skLineSegment(sketch, "E279", {"start": v(22.06, -20.03) * mm, "end": v(22.46, -20.07) * mm});
            skLineSegment(sketch, "E280", {"start": v(22.46, -20.07) * mm, "end": v(23.13, -19.92) * mm});
            skLineSegment(sketch, "E281", {"start": v(23.13, -19.92) * mm, "end": v(23.48, -19.99) * mm});
            skLineSegment(sketch, "E282", {"start": v(23.48, -19.99) * mm, "end": v(23.64, -20.26) * mm});
            skLineSegment(sketch, "E283", {"start": v(23.64, -20.26) * mm, "end": v(23.59, -20.37) * mm});
            skLineSegment(sketch, "E284", {"start": v(23.59, -20.37) * mm, "end": v(23.22, -20.45) * mm});
            skLineSegment(sketch, "E285", {"start": v(23.22, -20.45) * mm, "end": v(22.47, -20.45) * mm});
            skLineSegment(sketch, "E286", {"start": v(22.47, -20.45) * mm, "end": v(21.92, -20.52) * mm});
            skLineSegment(sketch, "E287", {"start": v(21.92, -20.52) * mm, "end": v(21.56, -20.72) * mm});
            skLineSegment(sketch, "E288", {"start": v(21.56, -20.72) * mm, "end": v(21.31, -20) * mm});
            skLineSegment(sketch, "E289", {"start": v(21.31, -20) * mm, "end": v(21.4, -18.92) * mm});
            skLineSegment(sketch, "E290", {"start": v(21.4, -18.92) * mm, "end": v(21.5, -18.15) * mm});
            skLineSegment(sketch, "E291", {"start": v(21.5, -18.15) * mm, "end": v(21.36, -17.74) * mm});
            skLineSegment(sketch, "E292", {"start": v(21.36, -17.74) * mm, "end": v(22.17, -16.64) * mm});
            skLineSegment(sketch, "E293", {"start": v(22.17, -16.64) * mm, "end": v(20.52, -17.28) * mm});
            skLineSegment(sketch, "E294", {"start": v(20.52, -17.28) * mm, "end": v(20.13, -17.24) * mm});
            skLineSegment(sketch, "E295", {"start": v(20.13, -17.24) * mm, "end": v(19.9, -16.99) * mm});
            skLineSegment(sketch, "E296", {"start": v(19.9, -16.99) * mm, "end": v(19.86, -16.72) * mm});
            skLineSegment(sketch, "E297", {"start": v(19.86, -16.72) * mm, "end": v(20.42, -16.72) * mm});
            skLineSegment(sketch, "E298", {"start": v(20.42, -16.72) * mm, "end": v(21.44, -16.4) * mm});
            skLineSegment(sketch, "E299", {"start": v(21.44, -16.4) * mm, "end": v(22.49, -15.68) * mm});
            skLineSegment(sketch, "E300", {"start": v(22.49, -15.68) * mm, "end": v(23.37, -14.73) * mm});
            skLineSegment(sketch, "E301", {"start": v(23.37, -14.73) * mm, "end": v(23.3, -14.4) * mm});
            skLineSegment(sketch, "E302", {"start": v(23.3, -14.4) * mm, "end": v(23.25, -14.2) * mm});
            skLineSegment(sketch, "E303", {"start": v(23.25, -14.2) * mm, "end": v(23.32, -14.12) * mm});
            skLineSegment(sketch, "E304", {"start": v(23.32, -14.12) * mm, "end": v(23.3, -14.14) * mm});
            skLineSegment(sketch, "E305", {"start": v(17.92, -17.56) * mm, "end": v(18.37, -17.5) * mm});
            skLineSegment(sketch, "E306", {"start": v(18.37, -17.5) * mm, "end": v(18.87, -17.57) * mm});
            skLineSegment(sketch, "E307", {"start": v(18.87, -17.57) * mm, "end": v(19.4, -17.87) * mm});
            skLineSegment(sketch, "E308", {"start": v(19.4, -17.87) * mm, "end": v(19.62, -18.25) * mm});
            skLineSegment(sketch, "E309", {"start": v(19.62, -18.25) * mm, "end": v(19.62, -18.7) * mm});
            skLineSegment(sketch, "E310", {"start": v(19.62, -18.7) * mm, "end": v(19.35, -19.1) * mm});
            skLineSegment(sketch, "E311", {"start": v(19.35, -19.1) * mm, "end": v(19.81, -19.87) * mm});
            skLineSegment(sketch, "E312", {"start": v(19.81, -19.87) * mm, "end": v(19.92, -20.3) * mm});
            skLineSegment(sketch, "E313", {"start": v(19.92, -20.3) * mm, "end": v(19.83, -20.75) * mm});
            skLineSegment(sketch, "E314", {"start": v(19.83, -20.75) * mm, "end": v(19.54, -20.98) * mm});
            skLineSegment(sketch, "E315", {"start": v(19.54, -20.98) * mm, "end": v(20.5, -20.98) * mm});
            skLineSegment(sketch, "E316", {"start": v(20.5, -20.98) * mm, "end": v(21.95, -21.23) * mm});
            skLineSegment(sketch, "E317", {"start": v(21.95, -21.23) * mm, "end": v(23.5, -21.63) * mm});
            skLineSegment(sketch, "E318", {"start": v(23.5, -21.63) * mm, "end": v(24.66, -21.86) * mm});
            skLineSegment(sketch, "E319", {"start": v(24.66, -21.86) * mm, "end": v(25.72, -21.68) * mm});
            skLineSegment(sketch, "E320", {"start": v(25.72, -21.68) * mm, "end": v(26.18, -21.68) * mm});
            skLineSegment(sketch, "E321", {"start": v(26.18, -21.68) * mm, "end": v(26.63, -22) * mm});
            skLineSegment(sketch, "E322", {"start": v(26.63, -22) * mm, "end": v(25.88, -22.4) * mm});
            skLineSegment(sketch, "E323", {"start": v(25.88, -22.4) * mm, "end": v(24.68, -22.55) * mm});
            skLineSegment(sketch, "E324", {"start": v(24.68, -22.55) * mm, "end": v(23.55, -22.3) * mm});
            skLineSegment(sketch, "E325", {"start": v(23.55, -22.3) * mm, "end": v(21.7, -21.8) * mm});
            skLineSegment(sketch, "E326", {"start": v(21.7, -21.8) * mm, "end": v(20.37, -21.5) * mm});
            skLineSegment(sketch, "E327", {"start": v(20.37, -21.5) * mm, "end": v(18.67, -21.55) * mm});
            skLineSegment(sketch, "E328", {"start": v(18.67, -21.55) * mm, "end": v(18.34, -21.55) * mm});
            skLineSegment(sketch, "E329", {"start": v(18.34, -21.55) * mm, "end": v(18.03, -21.34) * mm});
            skLineSegment(sketch, "E330", {"start": v(18.03, -21.34) * mm, "end": v(18.03, -20.98) * mm});
            skLineSegment(sketch, "E331", {"start": v(18.03, -20.98) * mm, "end": v(18.49, -21.04) * mm});
            skLineSegment(sketch, "E332", {"start": v(18.49, -21.04) * mm, "end": v(19, -20.95) * mm});
            skLineSegment(sketch, "E333", {"start": v(19, -20.95) * mm, "end": v(19.34, -20.5) * mm});
            skLineSegment(sketch, "E334", {"start": v(19.34, -20.5) * mm, "end": v(19.34, -20.02) * mm});
            skLineSegment(sketch, "E335", {"start": v(19.34, -20.02) * mm, "end": v(18.85, -19.32) * mm});
            skLineSegment(sketch, "E336", {"start": v(18.85, -19.32) * mm, "end": v(18.75, -18.7) * mm});
            skLineSegment(sketch, "E337", {"start": v(18.75, -18.7) * mm, "end": v(18.93, -18.26) * mm});
            skLineSegment(sketch, "E338", {"start": v(18.93, -18.26) * mm, "end": v(18.7, -18.23) * mm});
            skLineSegment(sketch, "E339", {"start": v(18.7, -18.23) * mm, "end": v(18.32, -18.23) * mm});
            skLineSegment(sketch, "E340", {"start": v(18.32, -18.23) * mm, "end": v(18.03, -17.96) * mm});
            skLineSegment(sketch, "E341", {"start": v(18.03, -17.96) * mm, "end": v(17.92, -17.7) * mm});
            skLineSegment(sketch, "E342", {"start": v(17.92, -17.7) * mm, "end": v(17.92, -17.56) * mm});
            skSolve(sketch);
        }
        {
            var Q0;
            Q0=qCreatedBy(makeId("Top.planeOp"),FACE);
            var sketch = newSketch(context, id + "F4", { "sketchPlane" : qUnion([Q0])});
            skLineSegment(sketch, "E343", {"start": v(1.24, -8.08) * mm, "end": v(0.6, -10.68) * mm});
            skLineSegment(sketch, "E344", {"start": v(0.6, -10.68) * mm, "end": v(0.8, -13.42) * mm});
            skLineSegment(sketch, "E345", {"start": v(0.8, -13.42) * mm, "end": v(1.46, -16.79) * mm});
            skLineSegment(sketch, "E346", {"start": v(1.46, -16.79) * mm, "end": v(2.08, -18.59) * mm});
            skLineSegment(sketch, "E347", {"start": v(2.08, -18.59) * mm, "end": v(3.42, -16.04) * mm});
            skLineSegment(sketch, "E348", {"start": v(3.42, -16.04) * mm, "end": v(5.37, -13.67) * mm});
            skLineSegment(sketch, "E349", {"start": v(5.37, -13.67) * mm, "end": v(8.1, -11.56) * mm});
            skLineSegment(sketch, "E350", {"start": v(8.1, -11.56) * mm, "end": v(10.3, -9.57) * mm});
            skLineSegment(sketch, "E351", {"start": v(10.3, -9.57) * mm, "end": v(7.53, -12.75) * mm});
            skLineSegment(sketch, "E352", {"start": v(7.53, -12.75) * mm, "end": v(6.44, -14.42) * mm});
            skLineSegment(sketch, "E353", {"start": v(6.44, -14.42) * mm, "end": v(5.7, -16.31) * mm});
            skLineSegment(sketch, "E354", {"start": v(5.7, -16.31) * mm, "end": v(5.48, -18.17) * mm});
            skLineSegment(sketch, "E355", {"start": v(5.48, -18.17) * mm, "end": v(5.77, -20.27) * mm});
            skLineSegment(sketch, "E356", {"start": v(5.77, -20.27) * mm, "end": v(6.84, -22.95) * mm});
            skLineSegment(sketch, "E357", {"start": v(6.84, -22.95) * mm, "end": v(7.53, -24.92) * mm});
            skLineSegment(sketch, "E358", {"start": v(7.53, -24.92) * mm, "end": v(7.73, -26.42) * mm});
            skLineSegment(sketch, "E359", {"start": v(7.73, -26.42) * mm, "end": v(7.4, -28.08) * mm});
            skLineSegment(sketch, "E360", {"start": v(7.4, -28.08) * mm, "end": v(6.58, -30.19) * mm});
            skLineSegment(sketch, "E361", {"start": v(6.58, -30.19) * mm, "end": v(5.27, -31.39) * mm});
            skLineSegment(sketch, "E362", {"start": v(5.27, -31.39) * mm, "end": v(1.4, -33.32) * mm});
            skLineSegment(sketch, "E363", {"start": v(1.4, -33.32) * mm, "end": v(-2.27, -32.52) * mm});
            skLineSegment(sketch, "E364", {"start": v(-2.27, -32.52) * mm, "end": v(-5, -32.04) * mm});
            skLineSegment(sketch, "E365", {"start": v(-5, -32.04) * mm, "end": v(-6.54, -31.22) * mm});
            skLineSegment(sketch, "E366", {"start": v(-6.54, -31.22) * mm, "end": v(-7.66, -29.54) * mm});
            skLineSegment(sketch, "E367", {"start": v(-7.45, -30.1) * mm, "end": v(-7.66, -29.54) * mm});
            skLineSegment(sketch, "E368", {"start": v(-7.45, -30.1) * mm, "end": v(-7.45, -19.2) * mm});
            skLineSegment(sketch, "E369", {"start": v(-7.7, -20.1) * mm, "end": v(-7.45, -19.2) * mm});
            skLineSegment(sketch, "E370", {"start": v(-7.7, -20.1) * mm, "end": v(-7.3, -17.48) * mm});
            skLineSegment(sketch, "E371", {"start": v(-7.3, -17.48) * mm, "end": v(-7.25, -14.97) * mm});
            skLineSegment(sketch, "E372", {"start": v(-7.25, -14.97) * mm, "end": v(-7.46, -12.5) * mm});
            skLineSegment(sketch, "E373", {"start": v(-7.46, -12.5) * mm, "end": v(-5.88, -14.65) * mm});
            skLineSegment(sketch, "E374", {"start": v(-5.88, -14.65) * mm, "end": v(-4.38, -17.82) * mm});
            skLineSegment(sketch, "E375", {"start": v(-4.38, -17.82) * mm, "end": v(-3.02, -21.14) * mm});
            skLineSegment(sketch, "E376", {"start": v(-3.02, -21.14) * mm, "end": v(-2.24, -16.84) * mm});
            skLineSegment(sketch, "E377", {"start": v(-2.24, -16.84) * mm, "end": v(-1.01, -12.38) * mm});
            skLineSegment(sketch, "E378", {"start": v(-1.01, -12.38) * mm, "end": v(0.28, -9.09) * mm});
            skLineSegment(sketch, "E379", {"start": v(0.28, -9.09) * mm, "end": v(1.24, -8.08) * mm});
            skLineSegment(sketch, "E380", {"start": v(0.08, -13.06) * mm, "end": v(-0.14, -16.55) * mm});
            skLineSegment(sketch, "E381", {"start": v(-0.14, -16.55) * mm, "end": v(0.04, -19.02) * mm});
            skLineSegment(sketch, "E382", {"start": v(0.04, -19.02) * mm, "end": v(0.67, -21.45) * mm});
            skLineSegment(sketch, "E383", {"start": v(0.67, -21.45) * mm, "end": v(1.8, -23.26) * mm});
            skLineSegment(sketch, "E384", {"start": v(1.8, -23.26) * mm, "end": v(2.98, -19.82) * mm});
            skLineSegment(sketch, "E385", {"start": v(2.98, -19.82) * mm, "end": v(4.11, -17.89) * mm});
            skLineSegment(sketch, "E386", {"start": v(4.11, -17.89) * mm, "end": v(4.78, -17.18) * mm});
            skLineSegment(sketch, "E387", {"start": v(4.78, -17.18) * mm, "end": v(4.29, -18.9) * mm});
            skLineSegment(sketch, "E388", {"start": v(4.29, -18.9) * mm, "end": v(4.29, -20.97) * mm});
            skLineSegment(sketch, "E389", {"start": v(4.29, -20.97) * mm, "end": v(4.67, -22.9) * mm});
            skLineSegment(sketch, "E390", {"start": v(4.67, -22.9) * mm, "end": v(5.28, -25.16) * mm});
            skLineSegment(sketch, "E391", {"start": v(5.28, -25.16) * mm, "end": v(5.93, -27.19) * mm});
            skLineSegment(sketch, "E392", {"start": v(5.93, -27.19) * mm, "end": v(6.09, -28.74) * mm});
            skLineSegment(sketch, "E393", {"start": v(6.09, -28.74) * mm, "end": v(5.8, -30.27) * mm});
            skLineSegment(sketch, "E394", {"start": v(5.8, -30.27) * mm, "end": v(4.78, -31.48) * mm});
            skLineSegment(sketch, "E395", {"start": v(4.78, -31.48) * mm, "end": v(1.4, -33.34) * mm});
            skLineSegment(sketch, "E396", {"start": v(1.4, -33.34) * mm, "end": v(-2.75, -32.22) * mm});
            skLineSegment(sketch, "E397", {"start": v(-2.75, -32.22) * mm, "end": v(-5.09, -30.91) * mm});
            skLineSegment(sketch, "E398", {"start": v(-5.09, -30.91) * mm, "end": v(-6.75, -28.68) * mm});
            skLineSegment(sketch, "E399", {"start": v(-6.75, -28.68) * mm, "end": v(-7.09, -27) * mm});
            skLineSegment(sketch, "E400", {"start": v(-7.09, -27) * mm, "end": v(-6.56, -25.17) * mm});
            skLineSegment(sketch, "E401", {"start": v(-6.56, -25.17) * mm, "end": v(-5.84, -22.65) * mm});
            skLineSegment(sketch, "E402", {"start": v(-5.84, -22.65) * mm, "end": v(-5.68, -20.35) * mm});
            skLineSegment(sketch, "E403", {"start": v(-5.68, -20.35) * mm, "end": v(-5.79, -18.8) * mm});
            skLineSegment(sketch, "E404", {"start": v(-5.79, -18.8) * mm, "end": v(-4.63, -21.14) * mm});
            skLineSegment(sketch, "E405", {"start": v(-4.63, -21.14) * mm, "end": v(-3.35, -24.2) * mm});
            skLineSegment(sketch, "E406", {"start": v(-3.35, -24.2) * mm, "end": v(-2.77, -25.35) * mm});
            skLineSegment(sketch, "E407", {"start": v(-2.77, -25.35) * mm, "end": v(-2.16, -22.03) * mm});
            skLineSegment(sketch, "E408", {"start": v(-2.16, -22.03) * mm, "end": v(-1.18, -17.48) * mm});
            skLineSegment(sketch, "E409", {"start": v(-1.18, -17.48) * mm, "end": v(-0.63, -15.45) * mm});
            skLineSegment(sketch, "E410", {"start": v(-0.63, -15.45) * mm, "end": v(0.08, -13.06) * mm});
            skLineSegment(sketch, "E411", {"start": v(-0.48, -20.41) * mm, "end": v(-0.55, -21.25) * mm});
            skLineSegment(sketch, "E412", {"start": v(-0.55, -21.25) * mm, "end": v(-0.44, -22.48) * mm});
            skLineSegment(sketch, "E413", {"start": v(-0.44, -22.48) * mm, "end": v(0.05, -24.36) * mm});
            skLineSegment(sketch, "E414", {"start": v(0.05, -24.36) * mm, "end": v(1.47, -27.18) * mm});
            skLineSegment(sketch, "E415", {"start": v(1.47, -27.18) * mm, "end": v(2.12, -24.81) * mm});
            skLineSegment(sketch, "E416", {"start": v(2.12, -24.81) * mm, "end": v(2.7, -23.69) * mm});
            skLineSegment(sketch, "E417", {"start": v(2.7, -23.69) * mm, "end": v(3.6, -22.78) * mm});
            skLineSegment(sketch, "E418", {"start": v(3.6, -22.78) * mm, "end": v(3.27, -23.6) * mm});
            skLineSegment(sketch, "E419", {"start": v(3.27, -23.6) * mm, "end": v(3.2, -24.68) * mm});
            skLineSegment(sketch, "E420", {"start": v(3.2, -24.68) * mm, "end": v(3.47, -26.04) * mm});
            skLineSegment(sketch, "E421", {"start": v(3.47, -26.04) * mm, "end": v(4.09, -27.64) * mm});
            skLineSegment(sketch, "E422", {"start": v(4.09, -27.64) * mm, "end": v(4.57, -28.9) * mm});
            skLineSegment(sketch, "E423", {"start": v(4.57, -28.9) * mm, "end": v(4.9, -29.54) * mm});
            skLineSegment(sketch, "E424", {"start": v(4.9, -29.54) * mm, "end": v(4.63, -30.22) * mm});
            skLineSegment(sketch, "E425", {"start": v(4.63, -30.22) * mm, "end": v(3.32, -32.02) * mm});
            skLineSegment(sketch, "E426", {"start": v(3.32, -32.02) * mm, "end": v(1.4, -32.98) * mm});
            skLineSegment(sketch, "E427", {"start": v(1.4, -32.98) * mm, "end": v(-2.8, -31.59) * mm});
            skLineSegment(sketch, "E428", {"start": v(-2.8, -31.59) * mm, "end": v(-4.33, -30.54) * mm});
            skLineSegment(sketch, "E429", {"start": v(-4.33, -30.54) * mm, "end": v(-5.13, -29.35) * mm});
            skLineSegment(sketch, "E430", {"start": v(-5.13, -29.35) * mm, "end": v(-5.54, -27.8) * mm});
            skLineSegment(sketch, "E431", {"start": v(-5.54, -27.8) * mm, "end": v(-5.26, -26.07) * mm});
            skLineSegment(sketch, "E432", {"start": v(-5.26, -26.07) * mm, "end": v(-4.9, -24.2) * mm});
            skLineSegment(sketch, "E433", {"start": v(-4.9, -24.2) * mm, "end": v(-4.9, -22.83) * mm});
            skLineSegment(sketch, "E434", {"start": v(-4.9, -22.83) * mm, "end": v(-4.15, -24.33) * mm});
            skLineSegment(sketch, "E435", {"start": v(-4.15, -24.33) * mm, "end": v(-3.22, -25.6) * mm});
            skLineSegment(sketch, "E436", {"start": v(-3.22, -25.6) * mm, "end": v(-1.75, -27.32) * mm});
            skLineSegment(sketch, "E437", {"start": v(-1.75, -27.32) * mm, "end": v(-1.6, -24.8) * mm});
            skLineSegment(sketch, "E438", {"start": v(-1.6, -24.8) * mm, "end": v(-1.29, -22.7) * mm});
            skLineSegment(sketch, "E439", {"start": v(-1.29, -22.7) * mm, "end": v(-0.82, -21.04) * mm});
            skLineSegment(sketch, "E440", {"start": v(-0.82, -21.04) * mm, "end": v(-0.48, -20.41) * mm});
            skLineSegment(sketch, "E441", {"start": v(3.1, -27.02) * mm, "end": v(3.05, -28.04) * mm});
            skLineSegment(sketch, "E442", {"start": v(3.05, -28.04) * mm, "end": v(3.36, -29.63) * mm});
            skLineSegment(sketch, "E443", {"start": v(3.36, -29.63) * mm, "end": v(3.67, -30.8) * mm});
            skLineSegment(sketch, "E444", {"start": v(3.67, -30.8) * mm, "end": v(3.5, -31.76) * mm});
            skLineSegment(sketch, "E445", {"start": v(3.5, -31.76) * mm, "end": v(1.4, -32.81) * mm});
            skLineSegment(sketch, "E446", {"start": v(1.4, -32.81) * mm, "end": v(-1.3, -31.87) * mm});
            skLineSegment(sketch, "E447", {"start": v(-1.3, -31.87) * mm, "end": v(-2.93, -30.99) * mm});
            skLineSegment(sketch, "E448", {"start": v(-2.93, -30.99) * mm, "end": v(-3.75, -30.26) * mm});
            skLineSegment(sketch, "E449", {"start": v(-3.75, -30.26) * mm, "end": v(-4.1, -29.57) * mm});
            skLineSegment(sketch, "E450", {"start": v(-4.1, -29.57) * mm, "end": v(-4.2, -28.18) * mm});
            skLineSegment(sketch, "E451", {"start": v(-4.2, -28.18) * mm, "end": v(-4.2, -26.83) * mm});
            skLineSegment(sketch, "E452", {"start": v(-4.2, -26.83) * mm, "end": v(-4.62, -25.7) * mm});
            skLineSegment(sketch, "E453", {"start": v(-4.62, -25.7) * mm, "end": v(-3.54, -26.97) * mm});
            skLineSegment(sketch, "E454", {"start": v(-3.54, -26.97) * mm, "end": v(-1.36, -29.19) * mm});
            skLineSegment(sketch, "E455", {"start": v(-1.36, -29.19) * mm, "end": v(-0.66, -29.7) * mm});
            skLineSegment(sketch, "E456", {"start": v(-0.66, -29.7) * mm, "end": v(-0.56, -28.07) * mm});
            skLineSegment(sketch, "E457", {"start": v(-0.56, -28.07) * mm, "end": v(-0.22, -26.82) * mm});
            skLineSegment(sketch, "E458", {"start": v(-0.22, -26.82) * mm, "end": v(0.08, -28.32) * mm});
            skLineSegment(sketch, "E459", {"start": v(0.08, -28.32) * mm, "end": v(0.63, -29.44) * mm});
            skLineSegment(sketch, "E460", {"start": v(0.63, -29.44) * mm, "end": v(1.57, -30.78) * mm});
            skLineSegment(sketch, "E461", {"start": v(1.57, -30.78) * mm, "end": v(1.72, -28.9) * mm});
            skLineSegment(sketch, "E462", {"start": v(1.72, -28.9) * mm, "end": v(2.14, -27.82) * mm});
            skLineSegment(sketch, "E463", {"start": v(2.14, -27.82) * mm, "end": v(3.1, -27.02) * mm});
            skSolve(sketch);
        }
        {
            var Q0;
            Q0 = qSketchRegion(id + "F1", true);
            var Q1;
            Q1 = qSketchRegion(id + "F2", true);
            var Q2;
            Q2 = qSketchRegion(id + "F3", true);
            var Q3;
            Q3 = qSketchRegion(id + "F4", true);
            extrude(context, id + "F5", {"entities" : qUnion([Q0, Q1, Q2, Q3]), "depth" : 2.54 * mm, "offsetDistance" : 25.4 * mm});
        }
        {
            var Q0;
            Q0=makeQuery(id+"F0.imprint","IMPRINT",FACE,{"disambiguationData":[TD([[makeQuery(id+"F0.imprint","IMPRINT",EDGE,{"derivedFrom":sQuery(id+"F0.wireOp",EDGE,"E0.0")}),-1.0]])]});
            extrude(context, id + "F6", {"entities" : qUnion([Q0]), "oppositeDirection" : true, "depth" : 3.8 * mm, "offsetDistance" : 25.4 * mm});
        }
        {
            var Q0;
            Q0=makeQuery(id+"F6.opExtrude","CAP_FACE",FACE,{"disambiguationData":[OSD([sQuery(id+"F0.wireOp",EDGE,"E0.0"),sQuery(id+"F0.wireOp",EDGE,"E0.1"),sQuery(id+"F0.wireOp",EDGE,"E0.2"),sQuery(id+"F0.wireOp",EDGE,"E1.0"),sQuery(id+"F0.wireOp",EDGE,"E1.1"),sQuery(id+"F0.wireOp",EDGE,"E1.2"),sQuery(id+"F0.wireOp",EDGE,"E2.trimOffspring"),sQuery(id+"F0.wireOp",EDGE,"E3.trimOffspring"),sQuery(id+"F0.wireOp",EDGE,"E4.trimOffspring"),sQuery(id+"F0.wireOp",EDGE,"E5.trimOffspring"),sQuery(id+"F0.wireOp",EDGE,"E6.trimOffspring"),sQuery(id+"F0.wireOp",EDGE,"E7.trimOffspring")])],"isStart":true});
            fillet(context, id + "F7", {"entities" : qUnion([Q0]), "radius" : 1.27 * mm, "tangentPropagation" : true, "allowEdgeOverflow" : false});
        }
    });
